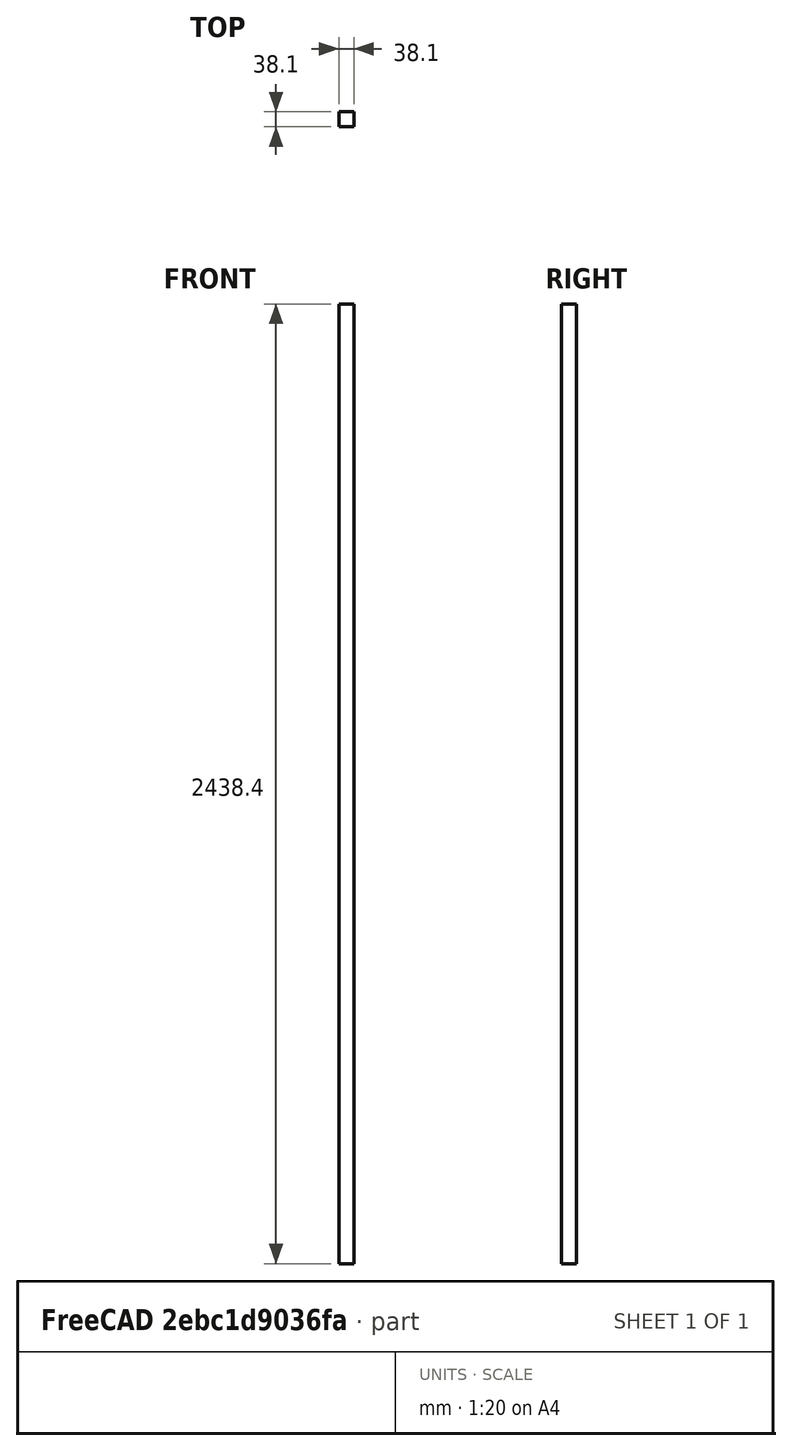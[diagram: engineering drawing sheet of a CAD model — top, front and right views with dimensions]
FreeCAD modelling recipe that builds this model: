
FCSTD DOCUMENT  (FreeCAD 0.21R33771 (Git))
Label: 2x2x8
License: All rights reserved
LicenseURL: http://en.wikipedia.org/wiki/All_rights_reserved
objects: Spreadsheet::Sheet×1, Sketcher::SketchObject×1, PartDesign::Pad×1, PartDesign::Body×1
note: 4 computed .brp shape members not serialized (recipe doc carries the construction recipe); baked Part::Feature solids carry a one-line shape summary decoded from their .brp

FEATURE [Spreadsheet::Sheet] Spreadsheet  label="var"
  cells = A2='varname; A3='len; B3(len)==25.4 * 8 * 12; A4='wid; B4(wid)==25.4 * 1.5; A5='thk; B5(thk)==wid
FEATURE [Sketcher::SketchObject] Sketch
  FullyConstrained = true
  MapMode = 5
  Support = -> [XY_Plane]
  expr: Constraints[10] = <<var>>.thk
  expr: Constraints[9] = <<var>>.wid
  sketch-geometry (4):
    g0: LineSegment StartX=-19.05 StartY=19.05 StartZ=0 EndX=19.05 EndY=19.05 EndZ=0
    g1: LineSegment StartX=19.05 StartY=19.05 StartZ=0 EndX=19.05 EndY=-19.05 EndZ=0
    g2: LineSegment StartX=19.05 StartY=-19.05 StartZ=0 EndX=-19.05 EndY=-19.05 EndZ=0
    g3: LineSegment StartX=-19.05 StartY=-19.05 StartZ=0 EndX=-19.05 EndY=19.05 EndZ=0
  constraints (11):
    c: Coincident(g0,g1)
    c: Coincident(g1,g2)
    c: Coincident(g2,g3)
    c: Coincident(g3,g0)
    c: Horizontal(g0)
    c: Horizontal(g2)
    c: Vertical(g1)
    c: Vertical(g3)
    c: Symmetric(g0,g2,g-1)
    c: Distance(g0,g0) = 38.1
    c: Distance(g0,g1) = 38.1
FEATURE [PartDesign::Pad] Pad
  Direction = (0,0,1)
  Length = 2438.4
  Length2 = 10
  Profile = -> Sketch
  ReferenceAxis = -> Sketch [N_Axis]
  Type = 0
  expr: Length = <<var>>.len
FEATURE [PartDesign::Body] Body
  Group = -> [Sketch,Pad]
  Origin = -> Origin
  Tip = -> Pad
